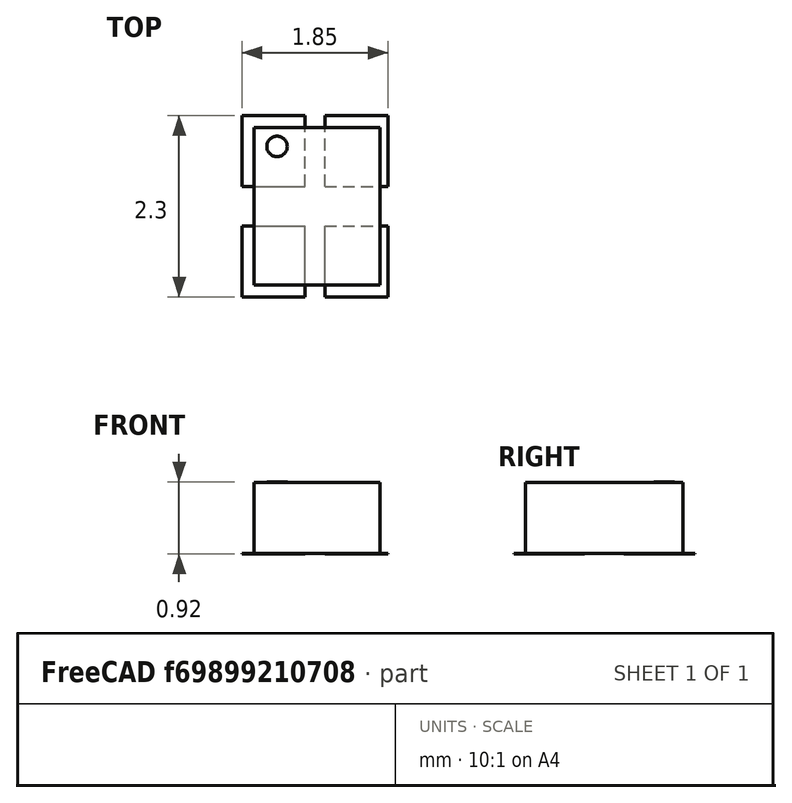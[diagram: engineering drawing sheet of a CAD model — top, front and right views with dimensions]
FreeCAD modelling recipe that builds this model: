
FCSTD DOCUMENT  (FreeCAD 0.17R11670 (Git))
Label: xtal-2016
License: All rights reserved
LicenseURL: http://en.wikipedia.org/wiki/All_rights_reserved
objects: Part::Box×5, Part::Cylinder×1, App::DocumentObjectGroup×1, Part::Feature×1
note: 7 computed .brp shape members not serialized (recipe doc carries the construction recipe); baked Part::Feature solids carry a one-line shape summary decoded from their .brp

FEATURE [Part::Box] Box  label="body-src"
  AttacherType = Attacher::AttachEngine3D
  Height = 0.9
  Length = 1.6
  Placement = pos=(-1.2,-0.5,-5.464e-08) rot=(0,0,1;0rad)
  Width = 2
FEATURE [Part::Box] Box001  label="pad-src"
  AttacherType = Attacher::AttachEngine3D
  Height = 0.01
  Length = 0.8
  Placement = pos=(-0.3,0.75,-0.00999995) rot=(0,0,1;0rad)
  Width = 0.9
FEATURE [Part::Cylinder] Cylinder  label="mark-src"
  Angle = 360
  AttacherType = Attacher::AttachEngine3D
  Height = 0.01
  Placement = pos=(-0.906689,1.26044,0.9) rot=(0,0,1;0rad)
  Radius = 0.13
FEATURE [Part::Box] Box002  label="pad-src001"
  AttacherType = Attacher::AttachEngine3D
  Height = 0.01
  Length = 0.8
  Placement = pos=(-1.35,0.75,-0.00999995) rot=(0,0,1;0rad)
  Width = 0.9
FEATURE [Part::Box] Box003  label="pad-src002"
  AttacherType = Attacher::AttachEngine3D
  Height = 0.01
  Length = 0.8
  Placement = pos=(-1.35,-0.65,-0.00999995) rot=(0,0,1;0rad)
  Width = 0.9
FEATURE [Part::Box] Box004  label="pad-src003"
  AttacherType = Attacher::AttachEngine3D
  Height = 0.01
  Length = 0.8
  Placement = pos=(-0.3,-0.65,-0.00999995) rot=(0,0,1;0rad)
  Width = 0.9
FEATURE [App::DocumentObjectGroup] Group  label="src"
  Group = -> [Box,Box001,Cylinder,Box002,Box003,Box004]
FEATURE [Part::Feature] Shape  label="Crystal2016"
  shape: bbox 1.85 x 2.3 x 0.92 mm, 32 faces (baked)
